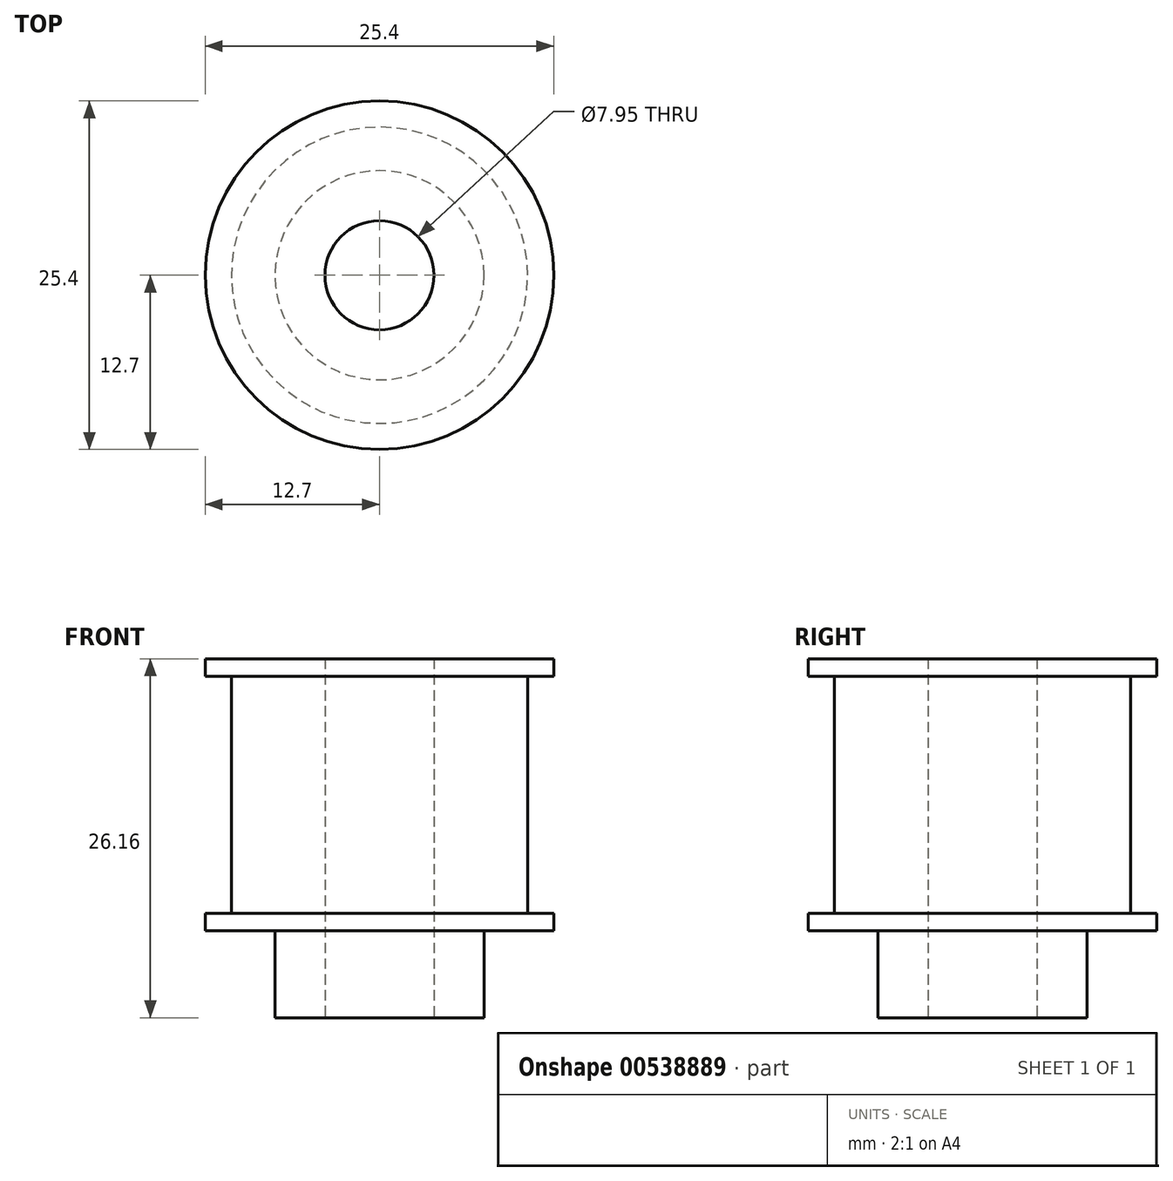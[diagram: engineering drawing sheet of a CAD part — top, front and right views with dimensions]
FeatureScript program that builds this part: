
annotation { "Feature Type Name" : "Feature", "Feature Type Description" : "" }
export const myFeature = defineFeature(function(context is Context, id is Id, definition is map)
    precondition{}
    {
        {
            var Q0;
            Q0=qCreatedBy(makeId("Top.planeOp"),FACE);
            var sketch = newSketch(context, id + "F0", { "sketchPlane" : qUnion([Q0])});
            skCircle(sketch, "E0", {"center": v(0, 0) * mm, "radius": 12.7 * mm});
            skCircle(sketch, "E1", {"center": v(0, 0) * mm, "radius": 3.98 * mm});
            skCircle(sketch, "E2", {"center": v(0, 0) * mm, "radius": 7.62 * mm});
            skCircle(sketch, "E3", {"center": v(0, 0) * mm, "radius": 10.8 * mm});
            skSolve(sketch);
        }
        {
            var Q0;
            Q0=makeQuery(id+"F0.imprint","IMPRINT",FACE,{"disambiguationData":[TD([[makeQuery(id+"F0.imprint","IMPRINT",EDGE,{"derivedFrom":sQuery(id+"F0.wireOp",EDGE,"E0")}),1.0]])]});
            extrude(context, id + "F1", {"entities" : qUnion([Q0]), "depth" : 1.27 * mm, "offsetDistance" : 25.4 * mm});
        }
        {
            var Q0;
            Q0=makeQuery(id+"F0.imprint","IMPRINT",FACE,{"disambiguationData":[TD([[makeQuery(id+"F0.imprint","IMPRINT",EDGE,{"derivedFrom":sQuery(id+"F0.wireOp",EDGE,"E2")}),-1.0]])]});
            var Q1;
            Q1=makeQuery(id+"F0.imprint","IMPRINT",FACE,{"disambiguationData":[TD([[makeQuery(id+"F0.imprint","IMPRINT",EDGE,{"derivedFrom":sQuery(id+"F0.wireOp",EDGE,"E1")}),-1.0]])]});
            extrude(context, id + "F2", {"entities" : qUnion([Q0, Q1]), "operationType" : NewBodyOperationType.ADD, "depth" : 19.8 * mm, "offsetDistance" : 25.4 * mm});
        }
        {
            var Q0;
            Q0=makeQuery(id+"F2.opExtrude","CAP_FACE",FACE,{"disambiguationData":[OSD([sQuery(id+"F0.wireOp",EDGE,"E1"),sQuery(id+"F0.wireOp",EDGE,"E3")])],"isStart":false});
            var sketch = newSketch(context, id + "F3", { "sketchPlane" : qUnion([Q0])});
            skCircle(sketch, "E4.0.0", {"center": v(0, 0) * mm, "radius": 12.7 * mm});
            skSolve(sketch);
        }
        {
            var Q0;
            Q0=makeQuery(id+"F3.imprint","IMPRINT",FACE,{"disambiguationData":[TD([[makeQuery(id+"F3.imprint","IMPRINT",EDGE,{"derivedFrom":sQuery(id+"F3.wireOp",EDGE,"E4.0.0")}),1.0]])]});
            extrude(context, id + "F4", {"entities" : qUnion([Q0]), "operationType" : NewBodyOperationType.ADD, "oppositeDirection" : true, "depth" : 1.27 * mm, "offsetDistance" : 25.4 * mm});
        }
        {
            var Q0;
            Q0=makeQuery(id+"F0.imprint","IMPRINT",FACE,{"disambiguationData":[TD([[makeQuery(id+"F0.imprint","IMPRINT",EDGE,{"derivedFrom":sQuery(id+"F0.wireOp",EDGE,"E1")}),-1.0]])]});
            extrude(context, id + "F5", {"entities" : qUnion([Q0]), "operationType" : NewBodyOperationType.ADD, "oppositeDirection" : true, "depth" : 6.35 * mm, "offsetDistance" : 25.4 * mm});
        }
    });
